# Revit family: Haworth_XSeries_CommonTop
name_source: partatom
category: Furniture Systems
revit_build: Autodesk Revit 2018 (Build: 20170223_1515(x64)
units: mm (PartAtom-declared; Revit-internal decimal feet)

## family parameters
Always vertical = Yes
Cut with Voids When Loaded = No
OmniClass Number = 23.40.70.14.64.21
OmniClass Title = Systems Furniture
Part Type = Normal
Room Calculation Point = No
Round Connector Dimension = Use Diameter
Shared = No
Work Plane-Based = No

## types (5) — shared parameters
Assembly Code = E2020200
Description = Haworth Masters File Top
Manufacturer = Haworth
Max. Depth = 37 1/2"
Max. Width = 120"
Min. Depth = 18"
Min. Width = 30"
Model = Haworth Masters File Top
Revision Number = 6
Size = Verify Final Dim. w/ Haworth
Standard Depth = 18, 18.75, 36, 37.5 in.
Standard Width = 30-120 in.
Sustainability Info = https://www.haworth.com
Top Thickness = 1 3/16"
URL = http://www.haworth.com
Warranty = http://www.haworth.com

## per-type parameters (varying)
| type | Actual Depth | Actual Width | Depth | URL - Product | Width |
| 18d 60w 1h - Proud Style | 18 3/4" | 60" | 18 3/4" | https://www.haworth.com | 60" |
| 18d 60w 1h - Inset Style | 18" | 60" | 18" | https://www.haworth.com | 60" |
| 36d 60w 1h - Inset Style | 36" | 60" | 36" | https://www.haworth.com | 60" |
| 36d 60w 1h - Proud Style | 37 1/2" | 60" | 37 1/2" | http://www.haworth.com | 60" |
| 18d 66w 1h - Proud Style | 18 3/4" | 66" | 18 3/4" | https://www.haworth.com | 66" |

## geometry (parser evidence)
native form markers: Sweep x2
no freeform markers — native parametric forms only
